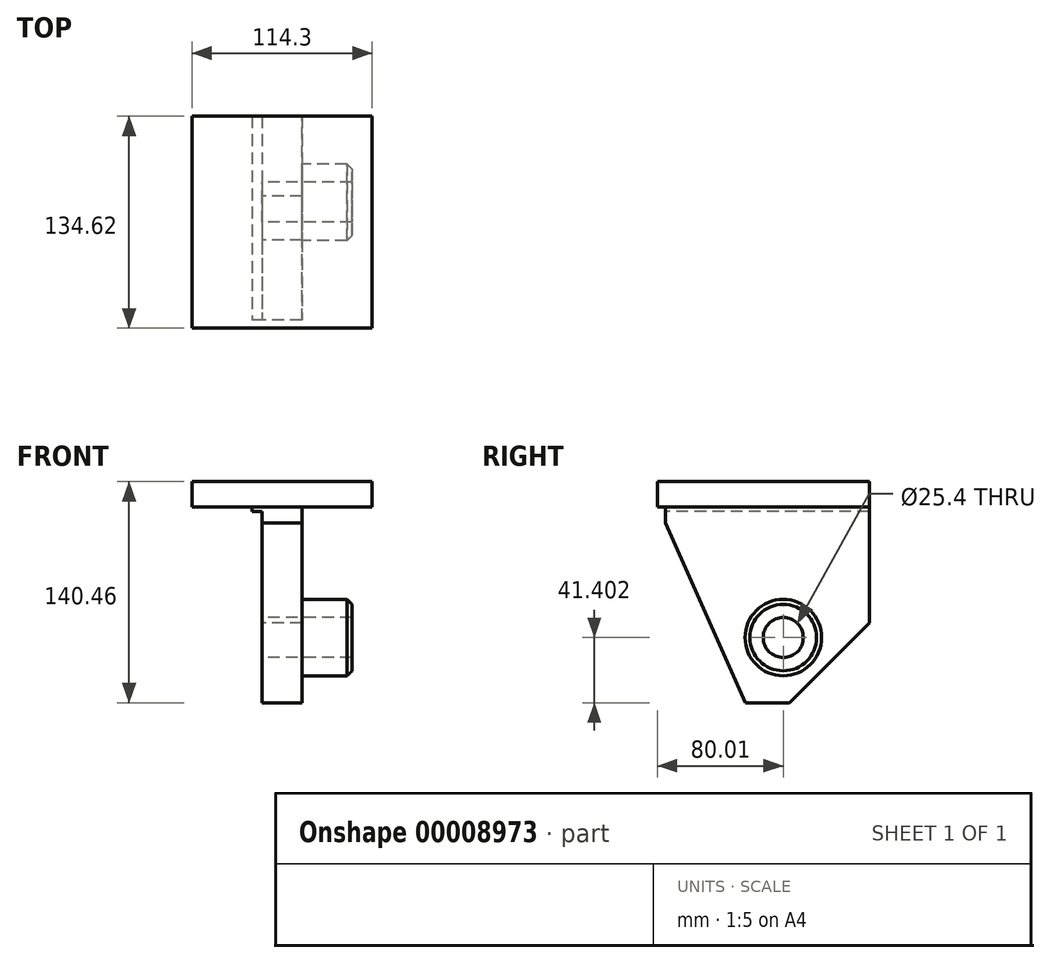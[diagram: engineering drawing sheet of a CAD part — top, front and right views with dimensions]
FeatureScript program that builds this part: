
annotation { "Feature Type Name" : "Feature", "Feature Type Description" : "" }
export const myFeature = defineFeature(function(context is Context, id is Id, definition is map)
    precondition{}
    {
        {
            var Q0;
            Q0=qCreatedBy(makeId("Right.planeOp"),FACE);
            var sketch = newSketch(context, id + "F0", { "sketchPlane" : qUnion([Q0])});
            skLineSegment(sketch, "E0", {"start": v(0, 0) * mm, "end": v(54.61, 0) * mm});
            skLineSegment(sketch, "E1", {"start": v(54.61, 0) * mm, "end": v(54.61, -73.66) * mm});
            skLineSegment(sketch, "E2", {"start": v(54.61, -73.66) * mm, "end": v(3.81, -124.46) * mm});
            skLineSegment(sketch, "E3", {"start": v(3.81, -124.46) * mm, "end": v(-24.13, -124.46) * mm});
            skLineSegment(sketch, "E4", {"start": v(-24.13, -124.46) * mm, "end": v(-74.93, -10.16) * mm});
            skLineSegment(sketch, "E5", {"start": v(-74.93, -10.16) * mm, "end": v(-74.93, 0) * mm});
            skLineSegment(sketch, "E6", {"start": v(-74.93, 0) * mm, "end": v(0, 0) * mm});
            skLineSegment(sketch, "E7", {"start": v(0, 0) * mm, "end": v(0, -83.06) * mm, "construction": true});
            skCircle(sketch, "E8", {"center": v(0, -83.06) * mm, "radius": 12.7 * mm});
            skSolve(sketch);
        }
        {
            var Q0;
            Q0 = qSketchRegion(id + "F0", true);
            extrude(context, id + "F1", {"entities" : qUnion([Q0]), "endBound" : BoundingType.SYMMETRIC, "depth" : 31.75 * mm});
        }
        {
            var Q0;
            Q0=qCreatedBy(makeId("Top.planeOp"),FACE);
            var sketch = newSketch(context, id + "F2", { "sketchPlane" : qUnion([Q0])});
            skLineSegment(sketch, "E9.0", {"start": v(60.33, -80) * mm, "end": v(60.33, 54.61) * mm});
            skLineSegment(sketch, "E10.0", {"start": v(-53.98, -80) * mm, "end": v(-53.98, 54.61) * mm});
            skLineSegment(sketch, "E11.0", {"start": v(60.33, -80) * mm, "end": v(-53.98, -80) * mm});
            skLineSegment(sketch, "E12.0", {"start": v(60.33, 54.61) * mm, "end": v(-53.98, 54.61) * mm});
            skPoint(sketch, "E13.orphan", {"position": v(-15.88, 54.61) * mm});
            skPoint(sketch, "E14.orphan", {"position": v(15.88, 54.61) * mm});
            skSolve(sketch);
        }
        {
            var Q0;
            Q0 = qSketchRegion(id + "F2", true);
            extrude(context, id + "F3", {"entities" : qUnion([Q0]), "operationType" : NewBodyOperationType.ADD, "depth" : 16 * mm});
        }
        {
            var Q0;
            Q0=makeQuery(id+"F1.opExtrude","CAP_FACE",FACE,{"disambiguationData":[OSD([sQuery(id+"F0.wireOp",EDGE,"E0"),sQuery(id+"F0.wireOp",EDGE,"E1"),sQuery(id+"F0.wireOp",EDGE,"E2"),sQuery(id+"F0.wireOp",EDGE,"E3"),sQuery(id+"F0.wireOp",EDGE,"E4"),sQuery(id+"F0.wireOp",EDGE,"E5"),sQuery(id+"F0.wireOp",EDGE,"E6"),sQuery(id+"F0.wireOp",EDGE,"E8")])],"isStart":false});
            var sketch = newSketch(context, id + "F4", { "sketchPlane" : qUnion([Q0])});
            skCircle(sketch, "E15", {"center": v(0, -83.06) * mm, "radius": 24.3 * mm});
            skCircle(sketch, "E16.0", {"center": v(0, -83.06) * mm, "radius": 12.7 * mm});
            skSolve(sketch);
        }
        {
            var Q0;
            Q0 = qSketchRegion(id + "F4", true);
            extrude(context, id + "F5", {"entities" : qUnion([Q0]), "operationType" : NewBodyOperationType.ADD, "depth" : 31.75 * mm});
        }
        {
            var Q0;
            Q0=makeQuery(id+"F1.opExtrude","SWEPT_FACE",FACE,{"disambiguationData":[OSD([sQuery(id+"F0.wireOp",EDGE,"E5")])]});
            var sketch = newSketch(context, id + "F6", { "sketchPlane" : qUnion([Q0])});
            skLineSegment(sketch, "E17.0", {"start": v(-9.52, -3.05) * mm, "end": v(-53.98, -3.05) * mm});
            skLineSegment(sketch, "E18.0", {"start": v(-9.53, -124.46) * mm, "end": v(-9.53, -3.05) * mm});
            skLineSegment(sketch, "E19", {"start": v(-53.98, -3.05) * mm, "end": v(-53.98, -124.46) * mm});
            skLineSegment(sketch, "E20", {"start": v(-53.98, -124.46) * mm, "end": v(-9.52, -124.46) * mm});
            skSolve(sketch);
        }
        {
            var Q0;
            Q0 = qSketchRegion(id + "F6", true);
            extrude(context, id + "F7", {"entities" : qUnion([Q0]), "operationType" : NewBodyOperationType.REMOVE, "endBound" : BoundingType.THROUGH_ALL, "oppositeDirection" : true, "depth" : 25.4 * mm});
        }
        {
            var Q0;
            Q0=makeQuery(id+"F5.opExtrude","CAP_EDGE",EDGE,{"disambiguationData":[OSD([sQuery(id+"F4.wireOp",EDGE,"E15")])],"isStart":false});
            chamfer(context, id + "F8", {"entities" : qUnion([Q0]), "width" : 3.17 * mm, "tangentPropagation" : true});
        }
    });
